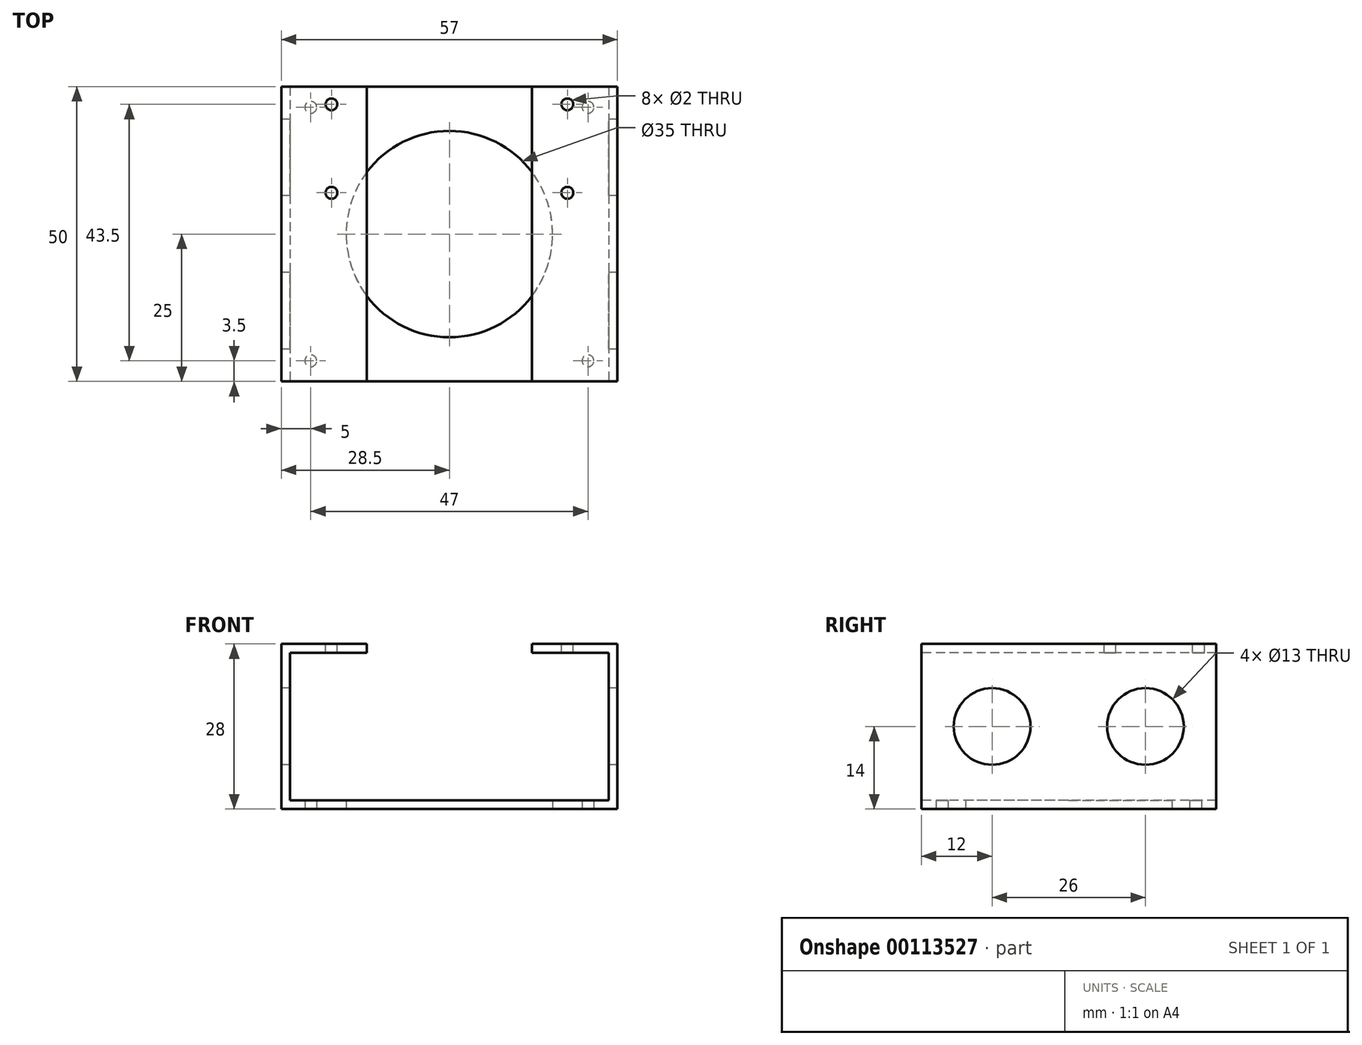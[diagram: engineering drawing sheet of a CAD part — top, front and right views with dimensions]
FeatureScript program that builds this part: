
annotation { "Feature Type Name" : "Feature", "Feature Type Description" : "" }
export const myFeature = defineFeature(function(context is Context, id is Id, definition is map)
    precondition{}
    {
        {
            var Q0;
            Q0=qCreatedBy(makeId("Top.planeOp"),FACE);
            var sketch = newSketch(context, id + "F0", { "sketchPlane" : qUnion([Q0])});
            skLineSegment(sketch, "E0.bottom", {"start": v(-27, 25) * mm, "end": v(27, 25) * mm});
            skLineSegment(sketch, "E0.top", {"start": v(-27, -25) * mm, "end": v(27, -25) * mm});
            skLineSegment(sketch, "E0.left", {"start": v(-27, 25) * mm, "end": v(-27, -25) * mm});
            skLineSegment(sketch, "E0.right", {"start": v(27, 25) * mm, "end": v(27, -25) * mm});
            skPoint(sketch, "E0.middle", {"position": v(0, 0) * mm});
            skLineSegment(sketch, "E1.bottom", {"start": v(-23.5, 21.5) * mm, "end": v(23.5, 21.5) * mm, "construction": true});
            skLineSegment(sketch, "E1.top", {"start": v(-23.5, -21.5) * mm, "end": v(23.5, -21.5) * mm, "construction": true});
            skLineSegment(sketch, "E1.left", {"start": v(-23.5, 21.5) * mm, "end": v(-23.5, -21.5) * mm, "construction": true});
            skLineSegment(sketch, "E1.right", {"start": v(23.5, 21.5) * mm, "end": v(23.5, -21.5) * mm, "construction": true});
            skCircle(sketch, "E2", {"center": v(-23.5, 21.5) * mm, "radius": 1 * mm});
            skCircle(sketch, "E3.MirrorC", {"center": v(23.5, 21.5) * mm, "radius": 1 * mm});
            skCircle(sketch, "E4.MirrorC", {"center": v(-23.5, -21.5) * mm, "radius": 1 * mm});
            skCircle(sketch, "E5.MirrorC", {"center": v(23.5, -21.5) * mm, "radius": 1 * mm});
            skSolve(sketch);
        }
        {
            var Q0;
            Q0=qSketchRegion(id+"F0",true);
            extrude(context, id + "F1", {"entities" : qUnion([Q0]), "depth" : 1.5 * mm});
        }
        {
            var Q0;
            Q0=qCreatedBy(makeId("Top.planeOp"),FACE);
            var sketch = newSketch(context, id + "F2", { "sketchPlane" : qUnion([Q0])});
            skLineSegment(sketch, "E6.0", {"start": v(27, 25) * mm, "end": v(27, -25) * mm, "construction": true});
            skLineSegment(sketch, "E7.bottom", {"start": v(27, 25) * mm, "end": v(28.5, 25) * mm});
            skLineSegment(sketch, "E7.top", {"start": v(27, -25) * mm, "end": v(28.5, -25) * mm});
            skLineSegment(sketch, "E7.left", {"start": v(27, 25) * mm, "end": v(27, -25) * mm});
            skLineSegment(sketch, "E7.right", {"start": v(28.5, 25) * mm, "end": v(28.5, -25) * mm});
            skSolve(sketch);
        }
        {
            var Q0;
            Q0=qSketchRegion(id+"F2",true);
            extrude(context, id + "F3", {"entities" : qUnion([Q0]), "operationType" : NewBodyOperationType.ADD, "depth" : (25 + 1.5 + 1.5) * mm});
        }
        {
            var Q0;
            Q0=makeQuery(id+"F3.opExtrude","SWEPT_FACE",FACE,{"disambiguationData":[OSD([sQuery(id+"F2.wireOp",EDGE,"E7.left")])]});
            var sketch = newSketch(context, id + "F4", { "sketchPlane" : qUnion([Q0])});
            skLineSegment(sketch, "E8.bottom", {"start": v(-25, 28) * mm, "end": v(25, 28) * mm});
            skLineSegment(sketch, "E8.top", {"start": v(-25, 26.5) * mm, "end": v(25, 26.5) * mm});
            skLineSegment(sketch, "E8.left", {"start": v(-25, 28) * mm, "end": v(-25, 26.5) * mm});
            skLineSegment(sketch, "E8.right", {"start": v(25, 28) * mm, "end": v(25, 26.5) * mm});
            skSolve(sketch);
        }
        {
            var Q0;
            Q0=qSketchRegion(id+"F4",true);
            extrude(context, id + "F5", {"entities" : qUnion([Q0]), "operationType" : NewBodyOperationType.ADD, "depth" : 13 * mm});
        }
        {
            var Q0;
            Q0=makeQuery(id+"F5.boolean.opBoolean","MERGE",FACE,{"derivedFrom":[makeQuery(id+"F3.opExtrude","CAP_FACE",FACE,{"disambiguationData":[OSD([sQuery(id+"F2.wireOp",EDGE,"E7.bottom"),sQuery(id+"F2.wireOp",EDGE,"E7.top"),sQuery(id+"F2.wireOp",EDGE,"E7.left"),sQuery(id+"F2.wireOp",EDGE,"E7.right")])],"isStart":false}),makeQuery(id+"F5.opExtrude","SWEPT_FACE",FACE,{"disambiguationData":[OSD([sQuery(id+"F4.wireOp",EDGE,"E8.bottom")])]})]});
            var sketch = newSketch(context, id + "F6", { "sketchPlane" : qUnion([Q0])});
            skCircle(sketch, "E9", {"center": v(20, 22) * mm, "radius": 1 * mm});
            skCircle(sketch, "E10", {"center": v(20, 7) * mm, "radius": 1 * mm});
            skSolve(sketch);
        }
        {
            var Q0;
            Q0=qSketchRegion(id+"F6",true);
            extrude(context, id + "F7", {"entities" : qUnion([Q0]), "operationType" : NewBodyOperationType.REMOVE, "endBound" : BoundingType.UP_TO_NEXT, "oppositeDirection" : true, "depth" : 25 * mm});
        }
        {
            var Q0;
            Q0=makeQuery(id+"F1.opExtrude","SWEPT_BODY",BODY,{"disambiguationData":[OSD([sQuery(id+"F0.wireOp",EDGE,"E0.bottom"),sQuery(id+"F0.wireOp",EDGE,"E0.top"),sQuery(id+"F0.wireOp",EDGE,"E0.left"),sQuery(id+"F0.wireOp",EDGE,"E0.right"),sQuery(id+"F0.wireOp",EDGE,"E2"),sQuery(id+"F0.wireOp",EDGE,"E3.MirrorC"),sQuery(id+"F0.wireOp",EDGE,"E4.MirrorC"),sQuery(id+"F0.wireOp",EDGE,"E5.MirrorC")])]});
            var Q1;
            Q1=qCreatedBy(makeId("Right.planeOp"),FACE);
            mirror(context, id + "F8", {"operationType" : NewBodyOperationType.ADD, "entities" : qUnion([Q0]), "mirrorPlane" : qUnion([Q1])});
        }
        {
            var Q0;
            Q0=makeQuery(id+"F8.opPattern","COPY",FACE,{"derivedFrom":makeQuery(id+"F3.opExtrude","SWEPT_FACE",FACE,{"disambiguationData":[OSD([sQuery(id+"F2.wireOp",EDGE,"E7.right")])]}),"instanceName":"1"});
            var sketch = newSketch(context, id + "F9", { "sketchPlane" : qUnion([Q0])});
            skLineSegment(sketch, "E11", {"start": v(-25, 14) * mm, "end": v(25, 14) * mm, "construction": true});
            skCircle(sketch, "E12", {"center": v(-13, 14) * mm, "radius": 6.5 * mm});
            skCircle(sketch, "E13.MirrorC", {"center": v(13, 14) * mm, "radius": 6.5 * mm});
            skSolve(sketch);
        }
        {
            var Q0;
            Q0=qSketchRegion(id+"F9",true);
            extrude(context, id + "F10", {"entities" : qUnion([Q0]), "operationType" : NewBodyOperationType.REMOVE, "endBound" : BoundingType.THROUGH_ALL, "oppositeDirection" : true, "depth" : 25 * mm});
        }
        {
            var Q0;
            {var subQ0=makeQuery(id+"F3.boolean.opBoolean","MERGE",FACE,{"derivedFrom":[makeQuery(id+"F1.opExtrude","CAP_FACE",FACE,{"disambiguationData":[OSD([sQuery(id+"F0.wireOp",EDGE,"E0.bottom"),sQuery(id+"F0.wireOp",EDGE,"E0.top"),sQuery(id+"F0.wireOp",EDGE,"E0.left"),sQuery(id+"F0.wireOp",EDGE,"E0.right"),sQuery(id+"F0.wireOp",EDGE,"E2"),sQuery(id+"F0.wireOp",EDGE,"E3.MirrorC"),sQuery(id+"F0.wireOp",EDGE,"E4.MirrorC"),sQuery(id+"F0.wireOp",EDGE,"E5.MirrorC")])],"isStart":true}),makeQuery(id+"F3.opExtrude","CAP_FACE",FACE,{"disambiguationData":[OSD([sQuery(id+"F2.wireOp",EDGE,"E7.bottom"),sQuery(id+"F2.wireOp",EDGE,"E7.top"),sQuery(id+"F2.wireOp",EDGE,"E7.left"),sQuery(id+"F2.wireOp",EDGE,"E7.right")])],"isStart":true})]});Q0=makeQuery(id+"F8.boolean.opBoolean","MERGE",FACE,{"derivedFrom":[subQ0,makeQuery(id+"F8.opPattern","COPY",FACE,{"derivedFrom":subQ0,"instanceName":"1"})]});}
            var sketch = newSketch(context, id + "F11", { "sketchPlane" : qUnion([Q0])});
            skCircle(sketch, "E14", {"center": v(0, 0) * mm, "radius": 17.5 * mm});
            skSolve(sketch);
        }
        {
            var Q0;
            Q0=qSketchRegion(id+"F11",true);
            extrude(context, id + "F12", {"entities" : qUnion([Q0]), "operationType" : NewBodyOperationType.REMOVE, "endBound" : BoundingType.UP_TO_NEXT, "oppositeDirection" : true, "depth" : 25 * mm});
        }
    });
